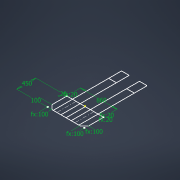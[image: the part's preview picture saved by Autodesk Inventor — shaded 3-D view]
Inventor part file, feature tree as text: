
AUTODESK INVENTOR PART (.ipt)
format: ipt  version: 2022 (Build 260153000, 153)  size: 106,496 bytes
history: native  units: mm
features: sketch x2
ambient origin geometry x8: Origin, YZ Plane, XZ Plane, XY Plane, X Axis, Y Axis, Z Axis, Center Point
feature tree (2):
  sketch  "Sketch1"  dims[d23=100.0mm]
  sketch  "Sketch2"  dims[d24=100.0mm d25=100.0mm d26=100.0mm d27=20.0mm d28=20.0mm d29=20.0mm d30=20.0mm d31=450.0mm d35=1600.0mm d36=300.0mm]
